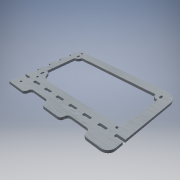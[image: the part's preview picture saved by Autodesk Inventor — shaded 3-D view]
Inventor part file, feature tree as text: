
AUTODESK INVENTOR PART (.ipt)
format: ipt  version: 2018.3 (Build 223284000, 284)  size: 252,416 bytes
history: native  units: mm
features: reference x16, other x5, extrude x3, sketch x3, fillet x2
ambient origin geometry x8: Origin, YZ Plane, XZ Plane, XY Plane, X Axis, Y Axis, Z Axis, Center Point
bodies: Solido1 (feature_tree)
feature tree (29):
  extrude  "Estrusione1"  Depth=165.0mm
  extrude  "Estrusione2"  Depth=33.0mm
  fillet  "Raccordo1"  Radius=10.0mm
  fillet  "Raccordo2"  Radius=33.0mm
  extrude  "Estrusione3"  Depth=10.0mm
  sketch  "Schizzo1"
  reference  "Riferimento4"
  reference  "Riferimento5"
  reference  "Riferimento6"
  reference  "Riferimento8"
  reference  "Riferimento9"
  reference  "Riferimento10"
  reference  "Riferimento11"
  reference  "Riferimento12"
  reference  "Riferimento13"
  reference  "Riferimento14"
  reference  "Riferimento15"
  sketch  "Schizzo2"
  sketch  "Schizzo3"
  reference  "Riferimento16"
  reference  "Riferimento17"
  reference  "Riferimento18"
  reference  "Riferimento19"
  reference  "Riferimento20"
  other  "<userpath>\Desktop\Scorbot Hardware\Case Board\caseHw.iam"
  other  "caseHw.iam"
  other  "LC600H-12:1"
  other  "tavolaBase:1"
  other  "Dietro:1"
